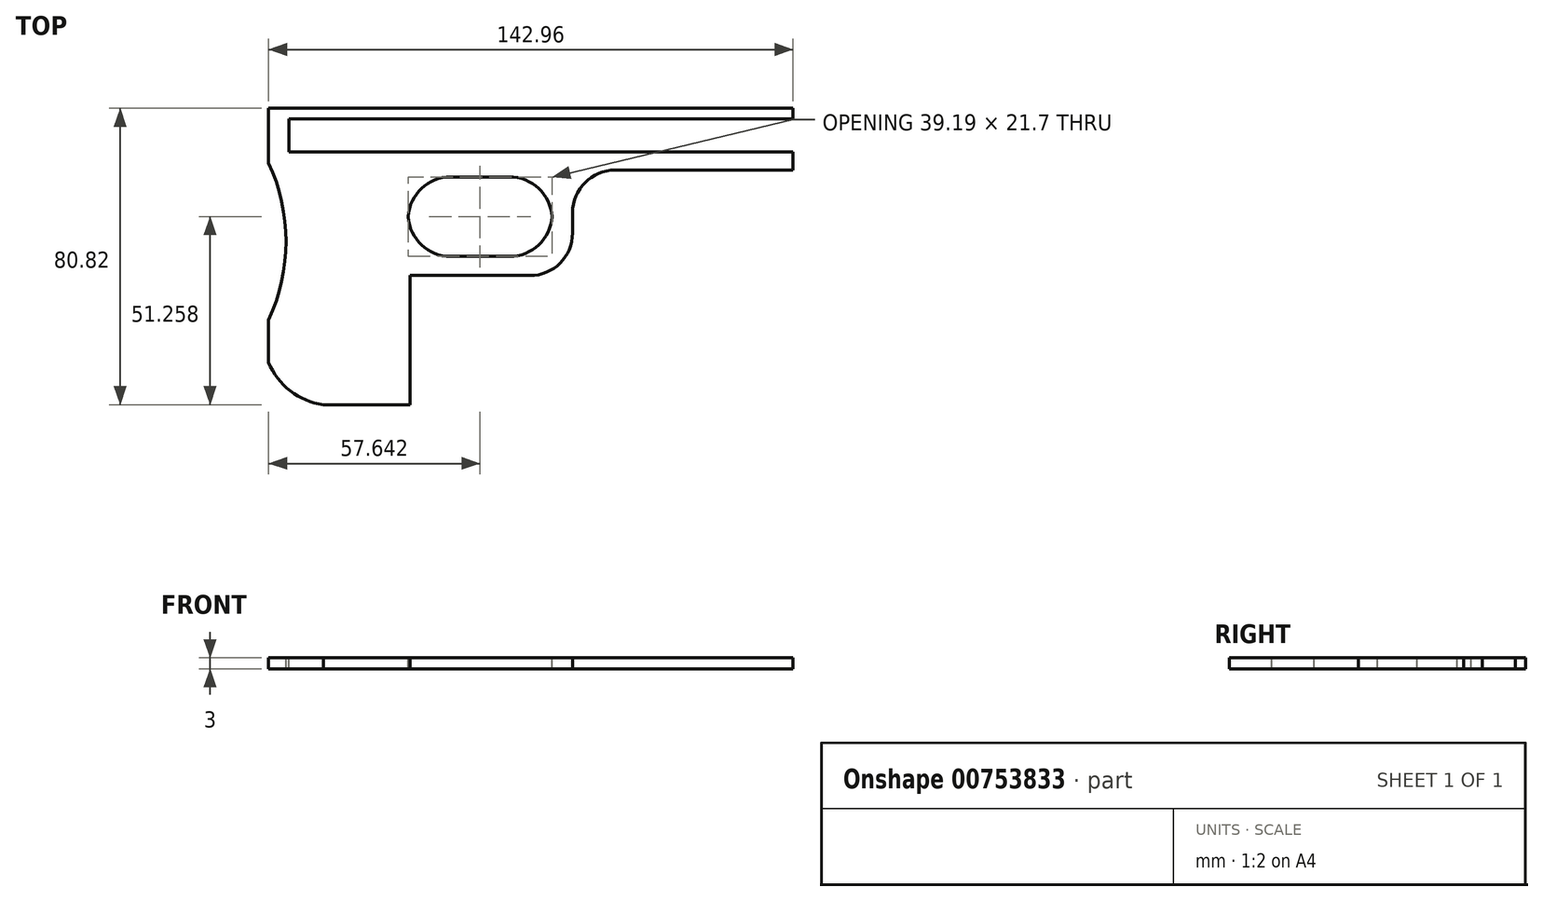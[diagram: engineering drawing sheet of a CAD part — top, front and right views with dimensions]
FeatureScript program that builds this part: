
annotation { "Feature Type Name" : "Feature", "Feature Type Description" : "" }
export const myFeature = defineFeature(function(context is Context, id is Id, definition is map)
    precondition{}
    {
        {
            var Q0;
            Q0=qCreatedBy(makeId("Top.planeOp"),FACE);
            var sketch = newSketch(context, id + "F0", { "sketchPlane" : qUnion([Q0])});
            skLineSegment(sketch, "E0.bottom", {"start": v(-71.48, -40.4) * mm, "end": v(71.48, -40.4) * mm});
            skLineSegment(sketch, "E0.top", {"start": v(-71.48, 40.4) * mm, "end": v(71.48, 40.4) * mm});
            skLineSegment(sketch, "E0.left", {"start": v(-71.48, -40.4) * mm, "end": v(-71.48, 40.4) * mm});
            skLineSegment(sketch, "E0.right", {"start": v(71.48, -40.4) * mm, "end": v(71.48, 40.4) * mm});
            skPoint(sketch, "E0.middle", {"position": v(0, 0) * mm});
            skSolve(sketch);
        }
        {
            var Q0;
            Q0=qSketchRegion(id+"F0",true);
            extrude(context, id + "F1", {"entities" : qUnion([Q0]), "depth" : 3 * mm, "offsetDistance" : 25 * mm});
        }
        {
            var Q0;
            Q0=makeQuery(id+"F1.opExtrude","CAP_FACE",FACE,{"disambiguationData":[OSD([sQuery(id+"F0.wireOp",EDGE,"E0.bottom"),sQuery(id+"F0.wireOp",EDGE,"E0.top"),sQuery(id+"F0.wireOp",EDGE,"E0.left"),sQuery(id+"F0.wireOp",EDGE,"E0.right")])],"isStart":false});
            var sketch = newSketch(context, id + "F2", { "sketchPlane" : qUnion([Q0])});
            skLineSegment(sketch, "E1.bottom", {"start": v(-65.97, 37.55) * mm, "end": v(71.48, 37.55) * mm});
            skLineSegment(sketch, "E1.top", {"start": v(-65.97, 28.57) * mm, "end": v(71.48, 28.57) * mm});
            skLineSegment(sketch, "E1.left", {"start": v(-65.97, 37.55) * mm, "end": v(-65.97, 28.57) * mm});
            skLineSegment(sketch, "E1.right", {"start": v(71.48, 37.55) * mm, "end": v(71.48, 28.57) * mm});
            skLineSegment(sketch, "E2.bottom", {"start": v(71.48, 23.55) * mm, "end": v(11.39, 23.55) * mm});
            skLineSegment(sketch, "E2.top", {"start": v(71.48, 5.05) * mm, "end": v(11.39, 5.05) * mm});
            skLineSegment(sketch, "E2.left", {"start": v(71.48, 23.55) * mm, "end": v(71.48, 5.05) * mm});
            skLineSegment(sketch, "E2.right", {"start": v(11.39, 23.55) * mm, "end": v(11.39, 5.05) * mm});
            skSolve(sketch);
        }
        {
            var Q0;
            Q0=qSketchRegion(id+"F2",true);
            extrude(context, id + "F3", {"entities" : qUnion([Q0]), "operationType" : NewBodyOperationType.REMOVE, "oppositeDirection" : true, "depth" : 52.3 * mm, "offsetDistance" : 25 * mm});
        }
        {
            var Q0;
            Q0=makeQuery(id+"F1.opExtrude","CAP_FACE",FACE,{"disambiguationData":[OSD([sQuery(id+"F0.wireOp",EDGE,"E0.bottom"),sQuery(id+"F0.wireOp",EDGE,"E0.top"),sQuery(id+"F0.wireOp",EDGE,"E0.left"),sQuery(id+"F0.wireOp",EDGE,"E0.right")])],"isStart":false});
            var sketch = newSketch(context, id + "F4", { "sketchPlane" : qUnion([Q0])});
            skLineSegment(sketch, "E3.bottom", {"start": v(-33.46, 21.7) * mm, "end": v(5.78, 21.7) * mm});
            skLineSegment(sketch, "E3.top", {"start": v(-33.46, 0) * mm, "end": v(5.78, 0) * mm});
            skLineSegment(sketch, "E3.left", {"start": v(-33.46, 21.7) * mm, "end": v(-33.46, 0) * mm});
            skLineSegment(sketch, "E3.right", {"start": v(5.78, 21.7) * mm, "end": v(5.78, 0) * mm});
            skSolve(sketch);
        }
        {
            var Q0;
            Q0=qSketchRegion(id+"F4",true);
            extrude(context, id + "F5", {"entities" : qUnion([Q0]), "operationType" : NewBodyOperationType.REMOVE, "oppositeDirection" : true, "depth" : 25 * mm, "offsetDistance" : 25 * mm});
        }
        {
            var Q0;
            Q0=makeQuery(id+"F1.opExtrude","CAP_FACE",FACE,{"disambiguationData":[OSD([sQuery(id+"F0.wireOp",EDGE,"E0.bottom"),sQuery(id+"F0.wireOp",EDGE,"E0.top"),sQuery(id+"F0.wireOp",EDGE,"E0.left"),sQuery(id+"F0.wireOp",EDGE,"E0.right")])],"isStart":false});
            var sketch = newSketch(context, id + "F6", { "sketchPlane" : qUnion([Q0])});
            skLineSegment(sketch, "E4.bottom", {"start": v(13.75, 0) * mm, "end": v(98.67, 0) * mm});
            skLineSegment(sketch, "E4.top", {"start": v(13.75, -55.24) * mm, "end": v(98.67, -55.24) * mm});
            skLineSegment(sketch, "E4.left", {"start": v(13.75, 0) * mm, "end": v(13.75, -55.24) * mm});
            skLineSegment(sketch, "E4.right", {"start": v(98.67, 0) * mm, "end": v(98.67, -55.24) * mm});
            skLineSegment(sketch, "E5.bottom", {"start": v(17.1, -5.2) * mm, "end": v(-27.22, -5.2) * mm});
            skLineSegment(sketch, "E5.top", {"start": v(17.1, -49.97) * mm, "end": v(-27.22, -49.97) * mm});
            skLineSegment(sketch, "E5.left", {"start": v(17.1, -5.2) * mm, "end": v(17.1, -49.97) * mm});
            skLineSegment(sketch, "E5.right", {"start": v(-27.22, -5.2) * mm, "end": v(-27.22, -49.97) * mm});
            skSolve(sketch);
        }
        {
            var Q0;
            Q0=qSketchRegion(id+"F6",true);
            extrude(context, id + "F7", {"entities" : qUnion([Q0]), "operationType" : NewBodyOperationType.REMOVE, "oppositeDirection" : true, "depth" : 25 * mm, "offsetDistance" : 25 * mm});
        }
        {
            var Q0;
            Q0=makeQuery(id+"F1.opExtrude","CAP_FACE",FACE,{"disambiguationData":[OSD([sQuery(id+"F0.wireOp",EDGE,"E0.bottom"),sQuery(id+"F0.wireOp",EDGE,"E0.top"),sQuery(id+"F0.wireOp",EDGE,"E0.left"),sQuery(id+"F0.wireOp",EDGE,"E0.right")])],"isStart":false});
            var sketch = newSketch(context, id + "F8", { "sketchPlane" : qUnion([Q0])});
            skLineSegment(sketch, "E6.bottom", {"start": v(11.39, 5.05) * mm, "end": v(114, 5.05) * mm});
            skLineSegment(sketch, "E6.top", {"start": v(11.39, -13.38) * mm, "end": v(114, -13.38) * mm});
            skLineSegment(sketch, "E6.left", {"start": v(11.39, 5.05) * mm, "end": v(11.39, -13.38) * mm});
            skLineSegment(sketch, "E6.right", {"start": v(114, 5.05) * mm, "end": v(114, -13.38) * mm});
            skSolve(sketch);
        }
        {
            var Q0;
            Q0=qSketchRegion(id+"F8",true);
            extrude(context, id + "F9", {"entities" : qUnion([Q0]), "operationType" : NewBodyOperationType.REMOVE, "oppositeDirection" : true, "depth" : 25 * mm, "offsetDistance" : 25 * mm});
        }
        {
            var Q0;
            Q0=makeQuery(id+"F9.boolean.opBoolean","INTERSECT",EDGE,{"derivedFrom":[makeQuery(id+"F7.boolean.opBoolean","COPY",FACE,{"derivedFrom":makeQuery(id+"F7.opExtrude","SWEPT_FACE",FACE,{"disambiguationData":[OSD([sQuery(id+"F6.wireOp",EDGE,"E5.bottom")])]})}),makeQuery(id+"F9.opExtrude","SWEPT_FACE",FACE,{"disambiguationData":[OSD([sQuery(id+"F8.wireOp",EDGE,"E6.left")])]})]});
            var Q1;
            Q1=makeQuery(id+"F3.boolean.opBoolean","COPY",EDGE,{"derivedFrom":makeQuery(id+"F3.opExtrude","SWEPT_EDGE",EDGE,{"disambiguationData":[OSD([sQuery(id+"F2.wireOp",EDGE,"E2.bottom"),sQuery(id+"F2.wireOp",EDGE,"E2.right")])]})});
            var Q2;
            Q2=makeQuery(id+"F7.boolean.opBoolean","COPY",EDGE,{"derivedFrom":makeQuery(id+"F7.opExtrude","SWEPT_EDGE",EDGE,{"disambiguationData":[OSD([sQuery(id+"F6.wireOp",EDGE,"E5.bottom"),sQuery(id+"F6.wireOp",EDGE,"E5.right")])]})});
            var Q3;
            Q3=makeQuery(id+"F5.boolean.opBoolean","COPY",EDGE,{"derivedFrom":makeQuery(id+"F5.opExtrude","SWEPT_EDGE",EDGE,{"disambiguationData":[OSD([sQuery(id+"F4.wireOp",EDGE,"E3.bottom"),sQuery(id+"F4.wireOp",EDGE,"E3.left")])]})});
            var Q4;
            Q4=makeQuery(id+"F5.boolean.opBoolean","COPY",EDGE,{"derivedFrom":makeQuery(id+"F5.opExtrude","SWEPT_EDGE",EDGE,{"disambiguationData":[OSD([sQuery(id+"F4.wireOp",EDGE,"E3.top"),sQuery(id+"F4.wireOp",EDGE,"E3.right")])]})});
            var Q5;
            Q5=makeQuery(id+"F5.boolean.opBoolean","COPY",EDGE,{"derivedFrom":makeQuery(id+"F5.opExtrude","SWEPT_EDGE",EDGE,{"disambiguationData":[OSD([sQuery(id+"F4.wireOp",EDGE,"E3.top"),sQuery(id+"F4.wireOp",EDGE,"E3.left")])]})});
            var Q6;
            Q6=makeQuery(id+"F5.boolean.opBoolean","COPY",EDGE,{"derivedFrom":makeQuery(id+"F5.opExtrude","SWEPT_EDGE",EDGE,{"disambiguationData":[OSD([sQuery(id+"F4.wireOp",EDGE,"E3.bottom"),sQuery(id+"F4.wireOp",EDGE,"E3.right")])]})});
            fillet(context, id + "F10", {"entities" : qUnion([Q0, Q1, Q2, Q3, Q4, Q5, Q6]), "radius" : 11.6 * mm, "tangentPropagation" : true, "allowEdgeOverflow" : false});
        }
        {
            var Q0;
            Q0=makeQuery(id+"F1.opExtrude","CAP_FACE",FACE,{"disambiguationData":[OSD([sQuery(id+"F0.wireOp",EDGE,"E0.bottom"),sQuery(id+"F0.wireOp",EDGE,"E0.top"),sQuery(id+"F0.wireOp",EDGE,"E0.left"),sQuery(id+"F0.wireOp",EDGE,"E0.right")])],"isStart":false});
            var sketch = newSketch(context, id + "F11", { "sketchPlane" : qUnion([Q0])});
            skArc(sketch, "E7", {"start": v(-71.48, -17.3) * mm, "mid": v(-66.77, 4.1) * mm, "end": v(-71.48, 25.5) * mm});
            skSolve(sketch);
        }
        {
            var Q0;
            Q0=qSketchRegion(id+"F11",true);
            var Q1;
            {var subQ0=sQuery(id+"F11.wireOp",EDGE,"E7");Q1=makeQuery(id+"F11.imprint","IMPRINT",FACE,{"disambiguationData":[TD([[makeQuery(id+"F11.imprint","IMPRINT",EDGE,{"derivedFrom":subQ0}),1.0]])]});}
            extrude(context, id + "F12", {"entities" : qUnion([Q0, Q1]), "operationType" : NewBodyOperationType.REMOVE, "oppositeDirection" : true, "depth" : 25 * mm, "offsetDistance" : 25 * mm});
        }
        {
            var Q0;
            Q0=makeQuery(id+"F1.opExtrude","CAP_FACE",FACE,{"disambiguationData":[OSD([sQuery(id+"F0.wireOp",EDGE,"E0.bottom"),sQuery(id+"F0.wireOp",EDGE,"E0.top"),sQuery(id+"F0.wireOp",EDGE,"E0.left"),sQuery(id+"F0.wireOp",EDGE,"E0.right")])],"isStart":false});
            var sketch = newSketch(context, id + "F13", { "sketchPlane" : qUnion([Q0])});
            skArc(sketch, "E8", {"start": v(-71.48, -28.86) * mm, "mid": v(-63.55, -38.02) * mm, "end": v(-51.66, -40.4) * mm});
            skArc(sketch, "E9", {"start": v(-32.9, -40.4) * mm, "mid": v(-27.36, -33.24) * mm, "end": v(-27.22, -24.18) * mm});
            skArc(sketch, "E10", {"start": v(-21.32, -6.7) * mm, "mid": v(-30.12, -13.47) * mm, "end": v(-27.22, -24.18) * mm});
            skSolve(sketch);
        }
        {
            var Q0;
            {var subQ0=sQuery(id+"F13.wireOp",EDGE,"E10");Q0=makeQuery(id+"F13.imprint","IMPRINT",FACE,{"disambiguationData":[TD([[makeQuery(id+"F13.imprint","IMPRINT",EDGE,{"derivedFrom":subQ0}),1.0]])]});}
            var Q1;
            {var subQ0=sQuery(id+"F13.wireOp",EDGE,"E9");var subQ1=makeQuery(id+"F1.opExtrude","CAP_EDGE",EDGE,{"disambiguationData":[OSD([sQuery(id+"F0.wireOp",EDGE,"E0.bottom")])],"isStart":false});var subQ2=makeQuery(id+"F13.imprint","INTERSECT",VERTEX,{"derivedFrom":[subQ1,subQ0]});Q1=makeQuery(id+"F13.imprint","IMPRINT",FACE,{"disambiguationData":[TD([[makeQuery(id+"F13.imprint","IMPRINT",EDGE,{"disambiguationData":[TD([[subQ2,-1.0]])],"derivedFrom":subQ0}),-1.0]])]});}
            var Q2;
            {var subQ0=sQuery(id+"F13.wireOp",EDGE,"E8");var subQ1=sQuery(id+"F0.wireOp",EDGE,"E0.bottom");var subQ5=makeQuery(id+"F1.opExtrude","CAP_EDGE",EDGE,{"disambiguationData":[OSD([subQ1])],"isStart":false});var subQ6=makeQuery(id+"F13.imprint","INTERSECT",VERTEX,{"disambiguationData":[OD(1.0)],"derivedFrom":[subQ5,subQ0]});Q2=makeQuery(id+"F13.imprint","IMPRINT",FACE,{"disambiguationData":[TD([[makeQuery(id+"F13.imprint","IMPRINT",EDGE,{"disambiguationData":[TD([[subQ6,1.0]])],"derivedFrom":subQ0}),-1.0]])]});}
            extrude(context, id + "F14", {"entities" : qUnion([Q0, Q1, Q2]), "operationType" : NewBodyOperationType.REMOVE, "oppositeDirection" : true, "depth" : 25 * mm, "offsetDistance" : 25 * mm});
        }
        {
            var Q0;
            Q0=makeQuery(id+"F1.opExtrude","CAP_FACE",FACE,{"disambiguationData":[OSD([sQuery(id+"F0.wireOp",EDGE,"E0.bottom"),sQuery(id+"F0.wireOp",EDGE,"E0.top"),sQuery(id+"F0.wireOp",EDGE,"E0.left"),sQuery(id+"F0.wireOp",EDGE,"E0.right")])],"isStart":false});
            var sketch = newSketch(context, id + "F15", { "sketchPlane" : qUnion([Q0])});
            skLineSegment(sketch, "E11", {"start": v(-32.9, -40.4) * mm, "end": v(-32.9, -5.2) * mm});
            skPoint(sketch, "E11.endSnap0", {"position": v(-7.92, -5.2) * mm});
            skLineSegment(sketch, "E12", {"start": v(-32.9, -5.2) * mm, "end": v(-7.92, -5.2) * mm});
            skSolve(sketch);
        }
        {
            var Q0;
            {var subQ3=sQuery(id+"F15.wireOp",EDGE,"E11");Q0=makeQuery(id+"F15.imprint","IMPRINT",FACE,{"disambiguationData":[TD([[makeQuery(id+"F15.imprint","IMPRINT",EDGE,{"derivedFrom":subQ3}),-1.0]])]});}
            extrude(context, id + "F16", {"entities" : qUnion([Q0]), "operationType" : NewBodyOperationType.REMOVE, "oppositeDirection" : true, "depth" : 25 * mm, "offsetDistance" : 25 * mm});
        }
    });
